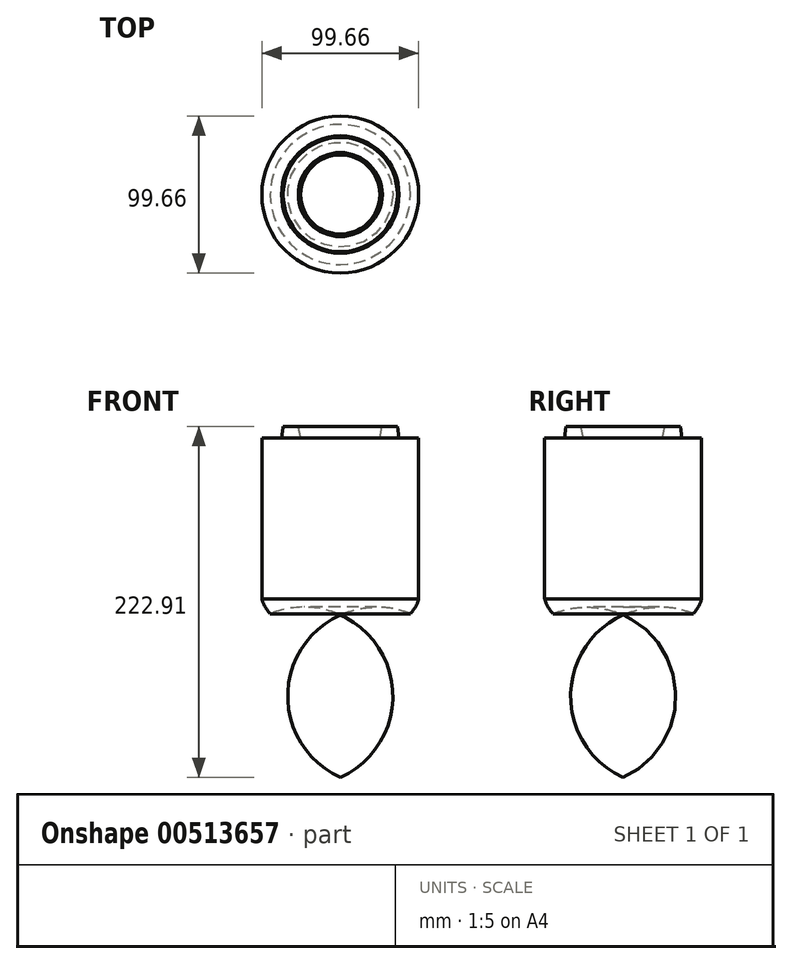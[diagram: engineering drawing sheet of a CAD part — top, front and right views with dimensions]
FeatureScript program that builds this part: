
annotation { "Feature Type Name" : "Feature", "Feature Type Description" : "" }
export const myFeature = defineFeature(function(context is Context, id is Id, definition is map)
    precondition{}
    {
        {
            var Q0;
            Q0=qCreatedBy(makeId("Right.planeOp"),FACE);
            var sketch = newSketch(context, id + "F0", { "sketchPlane" : qUnion([Q0])});
            skArc(sketch, "E0", {"start": v(44.51, -74.68) * mm, "mid": v(22.18, -70.5) * mm, "end": v(0, -75.44) * mm});
            skArc(sketch, "E1", {"start": v(44.51, -74.68) * mm, "mid": v(47.74, -70.26) * mm, "end": v(49.83, -65.19) * mm});
            skLineSegment(sketch, "E2", {"start": v(49.83, -65.19) * mm, "end": v(49.83, 36.92) * mm});
            skLineSegment(sketch, "E3", {"start": v(37.3, 36.92) * mm, "end": v(36.26, 44.26) * mm});
            skLineSegment(sketch, "E4", {"start": v(37.3, 36.92) * mm, "end": v(49.83, 36.92) * mm});
            skLineSegment(sketch, "E5", {"start": v(36.26, 44.26) * mm, "end": v(26.67, 44.26) * mm});
            skLineSegment(sketch, "E6", {"start": v(26.67, 44.26) * mm, "end": v(25.1, 36.92) * mm});
            skLineSegment(sketch, "E7", {"start": v(25.1, 36.92) * mm, "end": v(0, 36.92) * mm});
            skLineSegment(sketch, "E8", {"start": v(0, -75.44) * mm, "end": v(0, 36.92) * mm});
            skSolve(sketch);
        }
        {
            var Q0;
            Q0=makeQuery(id+"F0.imprint","IMPRINT",FACE,{"disambiguationData":[TD([[makeQuery(id+"F0.imprint","IMPRINT",EDGE,{"derivedFrom":sQuery(id+"F0.wireOp",EDGE,"E0")}),-1.0]])]});
            var Q1;
            Q1=sQuery(id+"F0.wireOp",EDGE,"E8");
            revolve(context, id + "F1", {"entities" : qUnion([Q0]), "axis" : qUnion([Q1]), "revolveType" : RevolveType.FULL});
        }
    });
